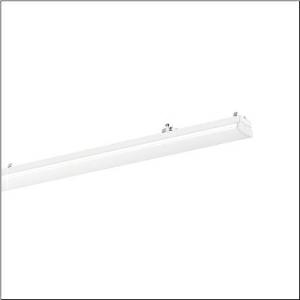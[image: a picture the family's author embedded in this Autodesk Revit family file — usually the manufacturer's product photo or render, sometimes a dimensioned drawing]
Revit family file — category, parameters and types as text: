
# Revit family: licross_21_recessed_opal_mo_52te1d7n46xg
name_source: partatom
category: Lighting Fixtures
units: mm (PartAtom-declared; Revit-internal decimal feet)

## family parameters
Cut with Voids When Loaded = No
Host = Face
Light Source = No
Part Type = Normal
Room Calculation Point = No
Round Connector Dimension = Use Diameter
Shared = No

## types (1)
- Licross 21 recessed opal MO (1 x LED, 6200 lm, 34.9 W, 4000K)
    Apparent Load = 35 VA
    CIE Flux Codes = 44 73 91 87 100
    Color Rendering = 80
    Color Temperature = 4000K
    Default Elevation = 1800 mm
    Description = Licross 21 recessed opal MO, luminaire insert, of sheet steel, galvanised, coil coated, white, length: 1.500mm, width: 66mm, height: 67mm, LED rated luminous flux: 6.200lm, light colour: 840, SDCM (Standard Deviation of Colour Matching)MacAdam ≤ 3 SDCM (initial), control gear: ON/OFF, with plug, 3-pole, with phase selection, mains connection: 220..240V, AC, 50/60Hz, rated input power: 35W, internal wiring halogen-free, primary optical cover: cover, of PMMA, light emission: direct with ceiling illumination distribution, primary light characteristic: symmetric, protection rating (complete): IP54, insulation class (complete): insulation class I (protective earthing), certification: CE, ENEC, VDE, UKCA, protection symbol: D if used in an environment with non-conductive dust loads with corresponding accessories, impact resistance: IK06, permissible ambient temperature for indoor applications: -35..+50°C, corresponds to IFS (International Featured Standards) requirements for safety and quality in the food industry, reducing of maximum allowable ambient temperature of 5°C with ceiling mounting, LABS conformity tested according to VDMA 24364:2018-05, The light source and the operating device comply with the requirements of the Ecodesign Regulation (EU) 2019/2020 and are replaceable in accordance with this regulation, packaging unit: 1 piece
    Height = 83 mm
    Lamp = 1 x LED
    Lamp Light Flux = 6200 lm
    Lamp Power = 34.9 W
    Lamp count = 1
    Length = 1500 mm
    Luminous efficacy = 178 lm/W
    Manufacturer = Siteco
    ModVariant = No
    Model = 52TE1D7N46XG
    Mounting Place = Ceiling
    Mounting Type = Pendant
    Number of Poles = 1
    OnlyDefault = Yes
    Power Factor = 1
    Product Name = Licross 21 recessed opal MO
    Product group = luminaire insert | ceiling pendant
    ProductGroupID = 901
    Protection Class = Protection class I
    Protection Degree = IP 54
    RLX_Detail_Level = 1
    RLX_Emergency_Light_Flux = 0 lm
    RLX_Emergency_Type = 0
    RLX_Emergency_Type_DB = No
    RlxData = <blob elided: 23349 chars, md5=30024a0f>
    Socket = socket
    Standby Power = 0 W
    System Light Flux = 6200 lm
    System Power = 35 W
    Type Comments = Product without accessories
    Type Image = l_1313666.jpg
    URL = http://relux.com
    VarID = ---
    Voltage = 0 V
    Weight = 0.00 kg
    Width = 76 mm

## geometry (parser evidence)
native form markers: Blend x4, Sweep x11
no freeform markers — native parametric forms only
